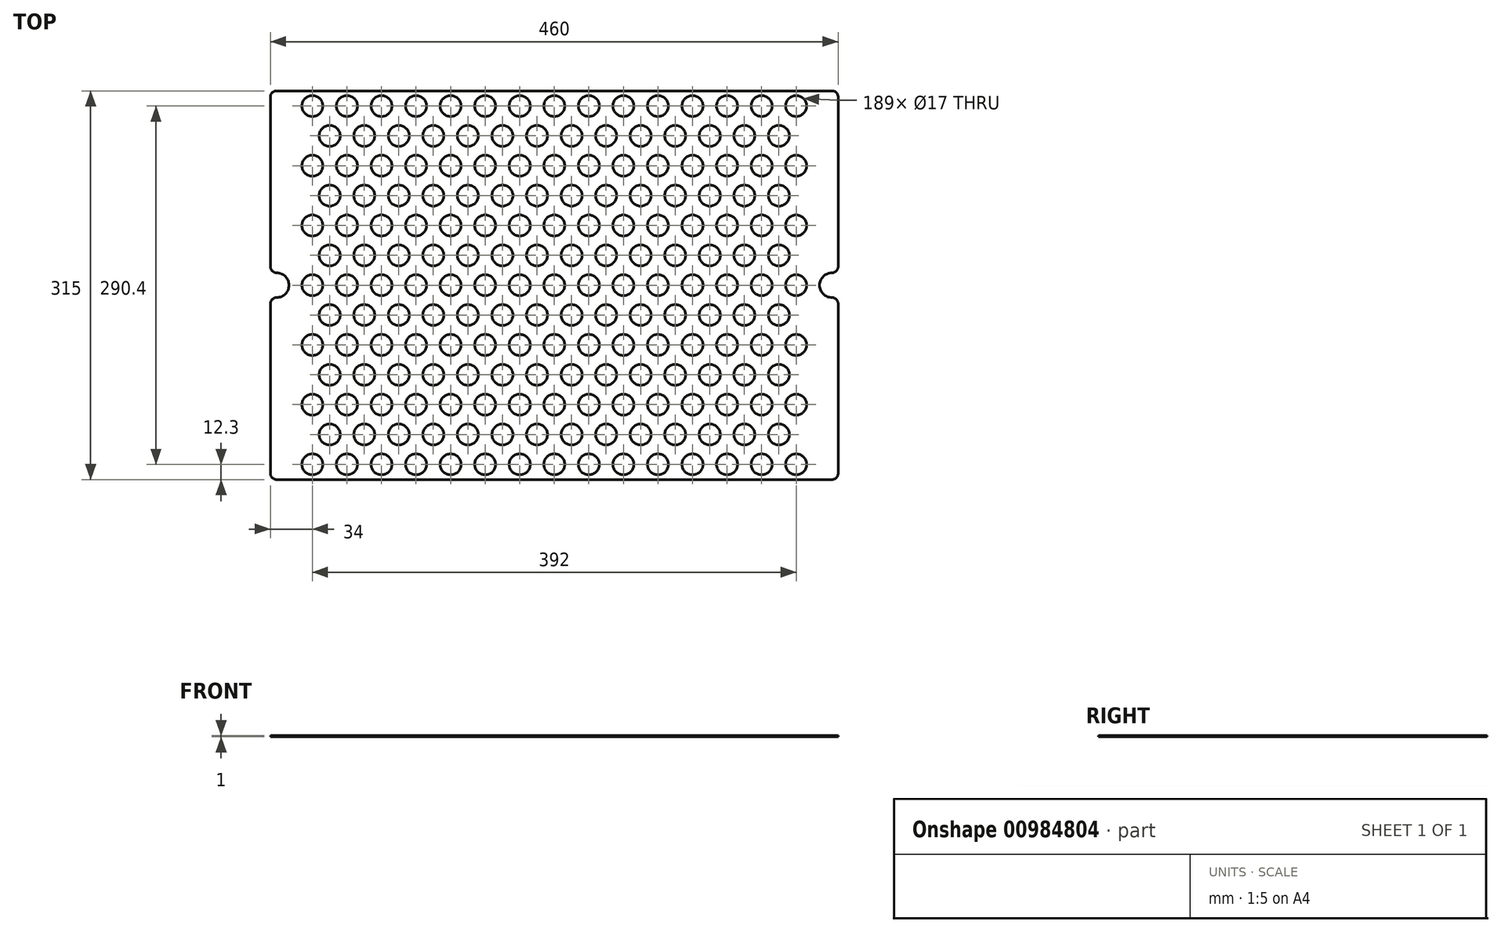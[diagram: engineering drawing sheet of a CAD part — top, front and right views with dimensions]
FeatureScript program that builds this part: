
annotation { "Feature Type Name" : "Feature", "Feature Type Description" : "" }
export const myFeature = defineFeature(function(context is Context, id is Id, definition is map)
    precondition{}
    {
        {
            var Q0;
            Q0=qCreatedBy(makeId("Top.planeOp"),FACE);
            var sketch = newSketch(context, id + "F0", { "sketchPlane" : qUnion([Q0])});
            skLineSegment(sketch, "E0.bottom", {"start": v(-225, 157.5) * mm, "end": v(225, 157.5) * mm});
            skLineSegment(sketch, "E0.top", {"start": v(-225, -157.5) * mm, "end": v(225, -157.5) * mm});
            skLineSegment(sketch, "E0.left", {"start": v(-230, 152.5) * mm, "end": v(-230, 15) * mm});
            skLineSegment(sketch, "E0.right", {"start": v(230, 152.5) * mm, "end": v(230, 15) * mm});
            skPoint(sketch, "E1.visualSharp", {"position": v(-230, 157.5) * mm});
            skArc(sketch, "E1.filletArc", {"start": v(-225, 157.5) * mm, "mid": v(-228.54, 156.04) * mm, "end": v(-230, 152.5) * mm});
            skPoint(sketch, "E2.visualSharp", {"position": v(230, 157.5) * mm});
            skArc(sketch, "E2.filletArc", {"start": v(230, 152.5) * mm, "mid": v(228.54, 156.04) * mm, "end": v(225, 157.5) * mm});
            skPoint(sketch, "E3.visualSharp", {"position": v(230, -157.5) * mm});
            skArc(sketch, "E3.filletArc", {"start": v(225, -157.5) * mm, "mid": v(228.54, -156.04) * mm, "end": v(230, -152.5) * mm});
            skPoint(sketch, "E4.visualSharp", {"position": v(-230, -157.5) * mm});
            skArc(sketch, "E4.filletArc", {"start": v(-230, -152.5) * mm, "mid": v(-228.54, -156.04) * mm, "end": v(-225, -157.5) * mm});
            skArc(sketch, "E5", {"start": v(-225, 10) * mm, "mid": v(-215, 0) * mm, "end": v(-225, -10) * mm});
            skArc(sketch, "E6", {"start": v(225, 10) * mm, "mid": v(215, 0) * mm, "end": v(225, -10) * mm});
            skLineSegment(sketch, "E7.trimOffspring", {"start": v(-230, -15) * mm, "end": v(-230, -152.5) * mm});
            skLineSegment(sketch, "E8.trimOffspring", {"start": v(230, -15) * mm, "end": v(230, -152.5) * mm});
            skPoint(sketch, "E9.visualSharp", {"position": v(230, 8.66) * mm});
            skArc(sketch, "E9.filletArc", {"start": v(225, 10) * mm, "mid": v(228.54, 11.46) * mm, "end": v(230, 15) * mm});
            skPoint(sketch, "E10.visualSharp", {"position": v(230, -8.66) * mm});
            skArc(sketch, "E10.filletArc", {"start": v(230, -15) * mm, "mid": v(228.54, -11.46) * mm, "end": v(225, -10) * mm});
            skPoint(sketch, "E11.visualSharp", {"position": v(-230, 8.66) * mm});
            skArc(sketch, "E11.filletArc", {"start": v(-230, 15) * mm, "mid": v(-228.54, 11.46) * mm, "end": v(-225, 10) * mm});
            skPoint(sketch, "E12.visualSharp", {"position": v(-230, -8.66) * mm});
            skArc(sketch, "E12.filletArc", {"start": v(-225, -10) * mm, "mid": v(-228.54, -11.46) * mm, "end": v(-230, -15) * mm});
            skCircle(sketch, "E13", {"center": v(-196, 145.2) * mm, "radius": 8.5 * mm});
            skCircle(sketch, "E14", {"center": v(-182, 121) * mm, "radius": 8.5 * mm});
            skCircle(sketch, "E15.0.1.0", {"center": v(-196, 96.8) * mm, "radius": 8.5 * mm});
            skCircle(sketch, "E15.0.2.0", {"center": v(-196, 48.4) * mm, "radius": 8.5 * mm});
            skCircle(sketch, "E15.0.3.0", {"center": v(-196, 0) * mm, "radius": 8.5 * mm});
            skCircle(sketch, "E15.0.4.0", {"center": v(-196, -48.4) * mm, "radius": 8.5 * mm});
            skCircle(sketch, "E15.0.5.0", {"center": v(-196, -96.8) * mm, "radius": 8.5 * mm});
            skCircle(sketch, "E15.0.6.0", {"center": v(-196, -145.2) * mm, "radius": 8.5 * mm});
            skCircle(sketch, "E15.1.0.0", {"center": v(-168, 145.2) * mm, "radius": 8.5 * mm});
            skCircle(sketch, "E15.1.1.0", {"center": v(-168, 96.8) * mm, "radius": 8.5 * mm});
            skCircle(sketch, "E15.1.2.0", {"center": v(-168, 48.4) * mm, "radius": 8.5 * mm});
            skCircle(sketch, "E15.1.3.0", {"center": v(-168, 0) * mm, "radius": 8.5 * mm});
            skCircle(sketch, "E15.1.4.0", {"center": v(-168, -48.4) * mm, "radius": 8.5 * mm});
            skCircle(sketch, "E15.1.5.0", {"center": v(-168, -96.8) * mm, "radius": 8.5 * mm});
            skCircle(sketch, "E15.1.6.0", {"center": v(-168, -145.2) * mm, "radius": 8.5 * mm});
            skCircle(sketch, "E15.2.0.0", {"center": v(-140, 145.2) * mm, "radius": 8.5 * mm});
            skCircle(sketch, "E15.2.1.0", {"center": v(-140, 96.8) * mm, "radius": 8.5 * mm});
            skCircle(sketch, "E15.2.2.0", {"center": v(-140, 48.4) * mm, "radius": 8.5 * mm});
            skCircle(sketch, "E15.2.3.0", {"center": v(-140, 0) * mm, "radius": 8.5 * mm});
            skCircle(sketch, "E15.2.4.0", {"center": v(-140, -48.4) * mm, "radius": 8.5 * mm});
            skCircle(sketch, "E15.2.5.0", {"center": v(-140, -96.8) * mm, "radius": 8.5 * mm});
            skCircle(sketch, "E15.2.6.0", {"center": v(-140, -145.2) * mm, "radius": 8.5 * mm});
            skCircle(sketch, "E15.3.0.0", {"center": v(-112, 145.2) * mm, "radius": 8.5 * mm});
            skCircle(sketch, "E15.3.1.0", {"center": v(-112, 96.8) * mm, "radius": 8.5 * mm});
            skCircle(sketch, "E15.3.2.0", {"center": v(-112, 48.4) * mm, "radius": 8.5 * mm});
            skCircle(sketch, "E15.3.3.0", {"center": v(-112, 0) * mm, "radius": 8.5 * mm});
            skCircle(sketch, "E15.3.4.0", {"center": v(-112, -48.4) * mm, "radius": 8.5 * mm});
            skCircle(sketch, "E15.3.5.0", {"center": v(-112, -96.8) * mm, "radius": 8.5 * mm});
            skCircle(sketch, "E15.3.6.0", {"center": v(-112, -145.2) * mm, "radius": 8.5 * mm});
            skCircle(sketch, "E15.4.0.0", {"center": v(-84, 145.2) * mm, "radius": 8.5 * mm});
            skCircle(sketch, "E15.4.1.0", {"center": v(-84, 96.8) * mm, "radius": 8.5 * mm});
            skCircle(sketch, "E15.4.2.0", {"center": v(-84, 48.4) * mm, "radius": 8.5 * mm});
            skCircle(sketch, "E15.4.3.0", {"center": v(-84, 0) * mm, "radius": 8.5 * mm});
            skCircle(sketch, "E15.4.4.0", {"center": v(-84, -48.4) * mm, "radius": 8.5 * mm});
            skCircle(sketch, "E15.4.5.0", {"center": v(-84, -96.8) * mm, "radius": 8.5 * mm});
            skCircle(sketch, "E15.4.6.0", {"center": v(-84, -145.2) * mm, "radius": 8.5 * mm});
            skCircle(sketch, "E15.5.0.0", {"center": v(-56, 145.2) * mm, "radius": 8.5 * mm});
            skCircle(sketch, "E15.5.1.0", {"center": v(-56, 96.8) * mm, "radius": 8.5 * mm});
            skCircle(sketch, "E15.5.2.0", {"center": v(-56, 48.4) * mm, "radius": 8.5 * mm});
            skCircle(sketch, "E15.5.3.0", {"center": v(-56, 0) * mm, "radius": 8.5 * mm});
            skCircle(sketch, "E15.5.4.0", {"center": v(-56, -48.4) * mm, "radius": 8.5 * mm});
            skCircle(sketch, "E15.5.5.0", {"center": v(-56, -96.8) * mm, "radius": 8.5 * mm});
            skCircle(sketch, "E15.5.6.0", {"center": v(-56, -145.2) * mm, "radius": 8.5 * mm});
            skCircle(sketch, "E15.6.0.0", {"center": v(-28, 145.2) * mm, "radius": 8.5 * mm});
            skCircle(sketch, "E15.6.1.0", {"center": v(-28, 96.8) * mm, "radius": 8.5 * mm});
            skCircle(sketch, "E15.6.2.0", {"center": v(-28, 48.4) * mm, "radius": 8.5 * mm});
            skCircle(sketch, "E15.6.3.0", {"center": v(-28, 0) * mm, "radius": 8.5 * mm});
            skCircle(sketch, "E15.6.4.0", {"center": v(-28, -48.4) * mm, "radius": 8.5 * mm});
            skCircle(sketch, "E15.6.5.0", {"center": v(-28, -96.8) * mm, "radius": 8.5 * mm});
            skCircle(sketch, "E15.6.6.0", {"center": v(-28, -145.2) * mm, "radius": 8.5 * mm});
            skCircle(sketch, "E15.7.0.0", {"center": v(0, 145.2) * mm, "radius": 8.5 * mm});
            skCircle(sketch, "E15.7.1.0", {"center": v(0, 96.8) * mm, "radius": 8.5 * mm});
            skCircle(sketch, "E15.7.2.0", {"center": v(0, 48.4) * mm, "radius": 8.5 * mm});
            skCircle(sketch, "E15.7.3.0", {"center": v(0, 0) * mm, "radius": 8.5 * mm});
            skCircle(sketch, "E15.7.4.0", {"center": v(0, -48.4) * mm, "radius": 8.5 * mm});
            skCircle(sketch, "E15.7.5.0", {"center": v(0, -96.8) * mm, "radius": 8.5 * mm});
            skCircle(sketch, "E15.7.6.0", {"center": v(0, -145.2) * mm, "radius": 8.5 * mm});
            skCircle(sketch, "E15.8.0.0", {"center": v(28, 145.2) * mm, "radius": 8.5 * mm});
            skCircle(sketch, "E15.8.1.0", {"center": v(28, 96.8) * mm, "radius": 8.5 * mm});
            skCircle(sketch, "E15.8.2.0", {"center": v(28, 48.4) * mm, "radius": 8.5 * mm});
            skCircle(sketch, "E15.8.3.0", {"center": v(28, 0) * mm, "radius": 8.5 * mm});
            skCircle(sketch, "E15.8.4.0", {"center": v(28, -48.4) * mm, "radius": 8.5 * mm});
            skCircle(sketch, "E15.8.5.0", {"center": v(28, -96.8) * mm, "radius": 8.5 * mm});
            skCircle(sketch, "E15.8.6.0", {"center": v(28, -145.2) * mm, "radius": 8.5 * mm});
            skCircle(sketch, "E15.9.0.0", {"center": v(56, 145.2) * mm, "radius": 8.5 * mm});
            skCircle(sketch, "E15.9.1.0", {"center": v(56, 96.8) * mm, "radius": 8.5 * mm});
            skCircle(sketch, "E15.9.2.0", {"center": v(56, 48.4) * mm, "radius": 8.5 * mm});
            skCircle(sketch, "E15.9.3.0", {"center": v(56, 0) * mm, "radius": 8.5 * mm});
            skCircle(sketch, "E15.9.4.0", {"center": v(56, -48.4) * mm, "radius": 8.5 * mm});
            skCircle(sketch, "E15.9.5.0", {"center": v(56, -96.8) * mm, "radius": 8.5 * mm});
            skCircle(sketch, "E15.9.6.0", {"center": v(56, -145.2) * mm, "radius": 8.5 * mm});
            skCircle(sketch, "E15.10.0.0", {"center": v(84, 145.2) * mm, "radius": 8.5 * mm});
            skCircle(sketch, "E15.10.1.0", {"center": v(84, 96.8) * mm, "radius": 8.5 * mm});
            skCircle(sketch, "E15.10.2.0", {"center": v(84, 48.4) * mm, "radius": 8.5 * mm});
            skCircle(sketch, "E15.10.3.0", {"center": v(84, 0) * mm, "radius": 8.5 * mm});
            skCircle(sketch, "E15.10.4.0", {"center": v(84, -48.4) * mm, "radius": 8.5 * mm});
            skCircle(sketch, "E15.10.5.0", {"center": v(84, -96.8) * mm, "radius": 8.5 * mm});
            skCircle(sketch, "E15.10.6.0", {"center": v(84, -145.2) * mm, "radius": 8.5 * mm});
            skCircle(sketch, "E15.11.0.0", {"center": v(112, 145.2) * mm, "radius": 8.5 * mm});
            skCircle(sketch, "E15.11.1.0", {"center": v(112, 96.8) * mm, "radius": 8.5 * mm});
            skCircle(sketch, "E15.11.2.0", {"center": v(112, 48.4) * mm, "radius": 8.5 * mm});
            skCircle(sketch, "E15.11.3.0", {"center": v(112, 0) * mm, "radius": 8.5 * mm});
            skCircle(sketch, "E15.11.4.0", {"center": v(112, -48.4) * mm, "radius": 8.5 * mm});
            skCircle(sketch, "E15.11.5.0", {"center": v(112, -96.8) * mm, "radius": 8.5 * mm});
            skCircle(sketch, "E15.11.6.0", {"center": v(112, -145.2) * mm, "radius": 8.5 * mm});
            skCircle(sketch, "E15.12.0.0", {"center": v(140, 145.2) * mm, "radius": 8.5 * mm});
            skCircle(sketch, "E15.12.1.0", {"center": v(140, 96.8) * mm, "radius": 8.5 * mm});
            skCircle(sketch, "E15.12.2.0", {"center": v(140, 48.4) * mm, "radius": 8.5 * mm});
            skCircle(sketch, "E15.12.3.0", {"center": v(140, 0) * mm, "radius": 8.5 * mm});
            skCircle(sketch, "E15.12.4.0", {"center": v(140, -48.4) * mm, "radius": 8.5 * mm});
            skCircle(sketch, "E15.12.5.0", {"center": v(140, -96.8) * mm, "radius": 8.5 * mm});
            skCircle(sketch, "E15.12.6.0", {"center": v(140, -145.2) * mm, "radius": 8.5 * mm});
            skCircle(sketch, "E15.13.0.0", {"center": v(168, 145.2) * mm, "radius": 8.5 * mm});
            skCircle(sketch, "E15.13.1.0", {"center": v(168, 96.8) * mm, "radius": 8.5 * mm});
            skCircle(sketch, "E15.13.2.0", {"center": v(168, 48.4) * mm, "radius": 8.5 * mm});
            skCircle(sketch, "E15.13.3.0", {"center": v(168, 0) * mm, "radius": 8.5 * mm});
            skCircle(sketch, "E15.13.4.0", {"center": v(168, -48.4) * mm, "radius": 8.5 * mm});
            skCircle(sketch, "E15.13.5.0", {"center": v(168, -96.8) * mm, "radius": 8.5 * mm});
            skCircle(sketch, "E15.13.6.0", {"center": v(168, -145.2) * mm, "radius": 8.5 * mm});
            skCircle(sketch, "E15.14.0.0", {"center": v(196, 145.2) * mm, "radius": 8.5 * mm});
            skCircle(sketch, "E15.14.1.0", {"center": v(196, 96.8) * mm, "radius": 8.5 * mm});
            skCircle(sketch, "E15.14.2.0", {"center": v(196, 48.4) * mm, "radius": 8.5 * mm});
            skCircle(sketch, "E15.14.3.0", {"center": v(196, 0) * mm, "radius": 8.5 * mm});
            skCircle(sketch, "E15.14.4.0", {"center": v(196, -48.4) * mm, "radius": 8.5 * mm});
            skCircle(sketch, "E15.14.5.0", {"center": v(196, -96.8) * mm, "radius": 8.5 * mm});
            skCircle(sketch, "E15.14.6.0", {"center": v(196, -145.2) * mm, "radius": 8.5 * mm});
            skLineSegment(sketch, "E15.direction1", {"start": v(-196, 145.2) * mm, "end": v(-168, 145.2) * mm, "construction": true});
            skLineSegment(sketch, "E15.direction2", {"start": v(-196, 145.2) * mm, "end": v(-196, 96.8) * mm, "construction": true});
            skCircle(sketch, "E16.0.1.0", {"center": v(-182, 72.6) * mm, "radius": 8.5 * mm});
            skCircle(sketch, "E16.0.2.0", {"center": v(-182, 24.2) * mm, "radius": 8.5 * mm});
            skCircle(sketch, "E16.0.3.0", {"center": v(-182, -24.2) * mm, "radius": 8.5 * mm});
            skCircle(sketch, "E16.0.4.0", {"center": v(-182, -72.6) * mm, "radius": 8.5 * mm});
            skCircle(sketch, "E16.0.5.0", {"center": v(-182, -121) * mm, "radius": 8.5 * mm});
            skCircle(sketch, "E16.1.0.0", {"center": v(-154, 121) * mm, "radius": 8.5 * mm});
            skCircle(sketch, "E16.1.1.0", {"center": v(-154, 72.6) * mm, "radius": 8.5 * mm});
            skCircle(sketch, "E16.1.2.0", {"center": v(-154, 24.2) * mm, "radius": 8.5 * mm});
            skCircle(sketch, "E16.1.3.0", {"center": v(-154, -24.2) * mm, "radius": 8.5 * mm});
            skCircle(sketch, "E16.1.4.0", {"center": v(-154, -72.6) * mm, "radius": 8.5 * mm});
            skCircle(sketch, "E16.1.5.0", {"center": v(-154, -121) * mm, "radius": 8.5 * mm});
            skCircle(sketch, "E16.2.0.0", {"center": v(-126, 121) * mm, "radius": 8.5 * mm});
            skCircle(sketch, "E16.2.1.0", {"center": v(-126, 72.6) * mm, "radius": 8.5 * mm});
            skCircle(sketch, "E16.2.2.0", {"center": v(-126, 24.2) * mm, "radius": 8.5 * mm});
            skCircle(sketch, "E16.2.3.0", {"center": v(-126, -24.2) * mm, "radius": 8.5 * mm});
            skCircle(sketch, "E16.2.4.0", {"center": v(-126, -72.6) * mm, "radius": 8.5 * mm});
            skCircle(sketch, "E16.2.5.0", {"center": v(-126, -121) * mm, "radius": 8.5 * mm});
            skCircle(sketch, "E16.3.0.0", {"center": v(-98, 121) * mm, "radius": 8.5 * mm});
            skCircle(sketch, "E16.3.1.0", {"center": v(-98, 72.6) * mm, "radius": 8.5 * mm});
            skCircle(sketch, "E16.3.2.0", {"center": v(-98, 24.2) * mm, "radius": 8.5 * mm});
            skCircle(sketch, "E16.3.3.0", {"center": v(-98, -24.2) * mm, "radius": 8.5 * mm});
            skCircle(sketch, "E16.3.4.0", {"center": v(-98, -72.6) * mm, "radius": 8.5 * mm});
            skCircle(sketch, "E16.3.5.0", {"center": v(-98, -121) * mm, "radius": 8.5 * mm});
            skCircle(sketch, "E16.4.0.0", {"center": v(-70, 121) * mm, "radius": 8.5 * mm});
            skCircle(sketch, "E16.4.1.0", {"center": v(-70, 72.6) * mm, "radius": 8.5 * mm});
            skCircle(sketch, "E16.4.2.0", {"center": v(-70, 24.2) * mm, "radius": 8.5 * mm});
            skCircle(sketch, "E16.4.3.0", {"center": v(-70, -24.2) * mm, "radius": 8.5 * mm});
            skCircle(sketch, "E16.4.4.0", {"center": v(-70, -72.6) * mm, "radius": 8.5 * mm});
            skCircle(sketch, "E16.4.5.0", {"center": v(-70, -121) * mm, "radius": 8.5 * mm});
            skCircle(sketch, "E16.5.0.0", {"center": v(-42, 121) * mm, "radius": 8.5 * mm});
            skCircle(sketch, "E16.5.1.0", {"center": v(-42, 72.6) * mm, "radius": 8.5 * mm});
            skCircle(sketch, "E16.5.2.0", {"center": v(-42, 24.2) * mm, "radius": 8.5 * mm});
            skCircle(sketch, "E16.5.3.0", {"center": v(-42, -24.2) * mm, "radius": 8.5 * mm});
            skCircle(sketch, "E16.5.4.0", {"center": v(-42, -72.6) * mm, "radius": 8.5 * mm});
            skCircle(sketch, "E16.5.5.0", {"center": v(-42, -121) * mm, "radius": 8.5 * mm});
            skCircle(sketch, "E16.6.0.0", {"center": v(-14, 121) * mm, "radius": 8.5 * mm});
            skCircle(sketch, "E16.6.1.0", {"center": v(-14, 72.6) * mm, "radius": 8.5 * mm});
            skCircle(sketch, "E16.6.2.0", {"center": v(-14, 24.2) * mm, "radius": 8.5 * mm});
            skCircle(sketch, "E16.6.3.0", {"center": v(-14, -24.2) * mm, "radius": 8.5 * mm});
            skCircle(sketch, "E16.6.4.0", {"center": v(-14, -72.6) * mm, "radius": 8.5 * mm});
            skCircle(sketch, "E16.6.5.0", {"center": v(-14, -121) * mm, "radius": 8.5 * mm});
            skCircle(sketch, "E16.7.0.0", {"center": v(14, 121) * mm, "radius": 8.5 * mm});
            skCircle(sketch, "E16.7.1.0", {"center": v(14, 72.6) * mm, "radius": 8.5 * mm});
            skCircle(sketch, "E16.7.2.0", {"center": v(14, 24.2) * mm, "radius": 8.5 * mm});
            skCircle(sketch, "E16.7.3.0", {"center": v(14, -24.2) * mm, "radius": 8.5 * mm});
            skCircle(sketch, "E16.7.4.0", {"center": v(14, -72.6) * mm, "radius": 8.5 * mm});
            skCircle(sketch, "E16.7.5.0", {"center": v(14, -121) * mm, "radius": 8.5 * mm});
            skCircle(sketch, "E16.8.0.0", {"center": v(42, 121) * mm, "radius": 8.5 * mm});
            skCircle(sketch, "E16.8.1.0", {"center": v(42, 72.6) * mm, "radius": 8.5 * mm});
            skCircle(sketch, "E16.8.2.0", {"center": v(42, 24.2) * mm, "radius": 8.5 * mm});
            skCircle(sketch, "E16.8.3.0", {"center": v(42, -24.2) * mm, "radius": 8.5 * mm});
            skCircle(sketch, "E16.8.4.0", {"center": v(42, -72.6) * mm, "radius": 8.5 * mm});
            skCircle(sketch, "E16.8.5.0", {"center": v(42, -121) * mm, "radius": 8.5 * mm});
            skCircle(sketch, "E16.9.0.0", {"center": v(70, 121) * mm, "radius": 8.5 * mm});
            skCircle(sketch, "E16.9.1.0", {"center": v(70, 72.6) * mm, "radius": 8.5 * mm});
            skCircle(sketch, "E16.9.2.0", {"center": v(70, 24.2) * mm, "radius": 8.5 * mm});
            skCircle(sketch, "E16.9.3.0", {"center": v(70, -24.2) * mm, "radius": 8.5 * mm});
            skCircle(sketch, "E16.9.4.0", {"center": v(70, -72.6) * mm, "radius": 8.5 * mm});
            skCircle(sketch, "E16.9.5.0", {"center": v(70, -121) * mm, "radius": 8.5 * mm});
            skCircle(sketch, "E16.10.0.0", {"center": v(98, 121) * mm, "radius": 8.5 * mm});
            skCircle(sketch, "E16.10.1.0", {"center": v(98, 72.6) * mm, "radius": 8.5 * mm});
            skCircle(sketch, "E16.10.2.0", {"center": v(98, 24.2) * mm, "radius": 8.5 * mm});
            skCircle(sketch, "E16.10.3.0", {"center": v(98, -24.2) * mm, "radius": 8.5 * mm});
            skCircle(sketch, "E16.10.4.0", {"center": v(98, -72.6) * mm, "radius": 8.5 * mm});
            skCircle(sketch, "E16.10.5.0", {"center": v(98, -121) * mm, "radius": 8.5 * mm});
            skCircle(sketch, "E16.11.0.0", {"center": v(126, 121) * mm, "radius": 8.5 * mm});
            skCircle(sketch, "E16.11.1.0", {"center": v(126, 72.6) * mm, "radius": 8.5 * mm});
            skCircle(sketch, "E16.11.2.0", {"center": v(126, 24.2) * mm, "radius": 8.5 * mm});
            skCircle(sketch, "E16.11.3.0", {"center": v(126, -24.2) * mm, "radius": 8.5 * mm});
            skCircle(sketch, "E16.11.4.0", {"center": v(126, -72.6) * mm, "radius": 8.5 * mm});
            skCircle(sketch, "E16.11.5.0", {"center": v(126, -121) * mm, "radius": 8.5 * mm});
            skCircle(sketch, "E16.12.0.0", {"center": v(154, 121) * mm, "radius": 8.5 * mm});
            skCircle(sketch, "E16.12.1.0", {"center": v(154, 72.6) * mm, "radius": 8.5 * mm});
            skCircle(sketch, "E16.12.2.0", {"center": v(154, 24.2) * mm, "radius": 8.5 * mm});
            skCircle(sketch, "E16.12.3.0", {"center": v(154, -24.2) * mm, "radius": 8.5 * mm});
            skCircle(sketch, "E16.12.4.0", {"center": v(154, -72.6) * mm, "radius": 8.5 * mm});
            skCircle(sketch, "E16.12.5.0", {"center": v(154, -121) * mm, "radius": 8.5 * mm});
            skCircle(sketch, "E16.13.0.0", {"center": v(182, 121) * mm, "radius": 8.5 * mm});
            skCircle(sketch, "E16.13.1.0", {"center": v(182, 72.6) * mm, "radius": 8.5 * mm});
            skCircle(sketch, "E16.13.2.0", {"center": v(182, 24.2) * mm, "radius": 8.5 * mm});
            skCircle(sketch, "E16.13.3.0", {"center": v(182, -24.2) * mm, "radius": 8.5 * mm});
            skCircle(sketch, "E16.13.4.0", {"center": v(182, -72.6) * mm, "radius": 8.5 * mm});
            skCircle(sketch, "E16.13.5.0", {"center": v(182, -121) * mm, "radius": 8.5 * mm});
            skLineSegment(sketch, "E16.direction1", {"start": v(-182, 121) * mm, "end": v(-154, 121) * mm, "construction": true});
            skLineSegment(sketch, "E16.direction2", {"start": v(-182, 121) * mm, "end": v(-182, 72.6) * mm, "construction": true});
            skSolve(sketch);
        }
        {
            var Q0;
            Q0=makeQuery(id+"F0.imprint","IMPRINT",FACE,{"disambiguationData":[TD([[makeQuery(id+"F0.imprint","IMPRINT",EDGE,{"derivedFrom":sQuery(id+"F0.wireOp",EDGE,"E0.bottom")}),-1.0]])]});
            extrude(context, id + "F1", {"entities" : qUnion([Q0]), "depth" : 1 * mm, "offsetDistance" : 25 * mm});
        }
    });
